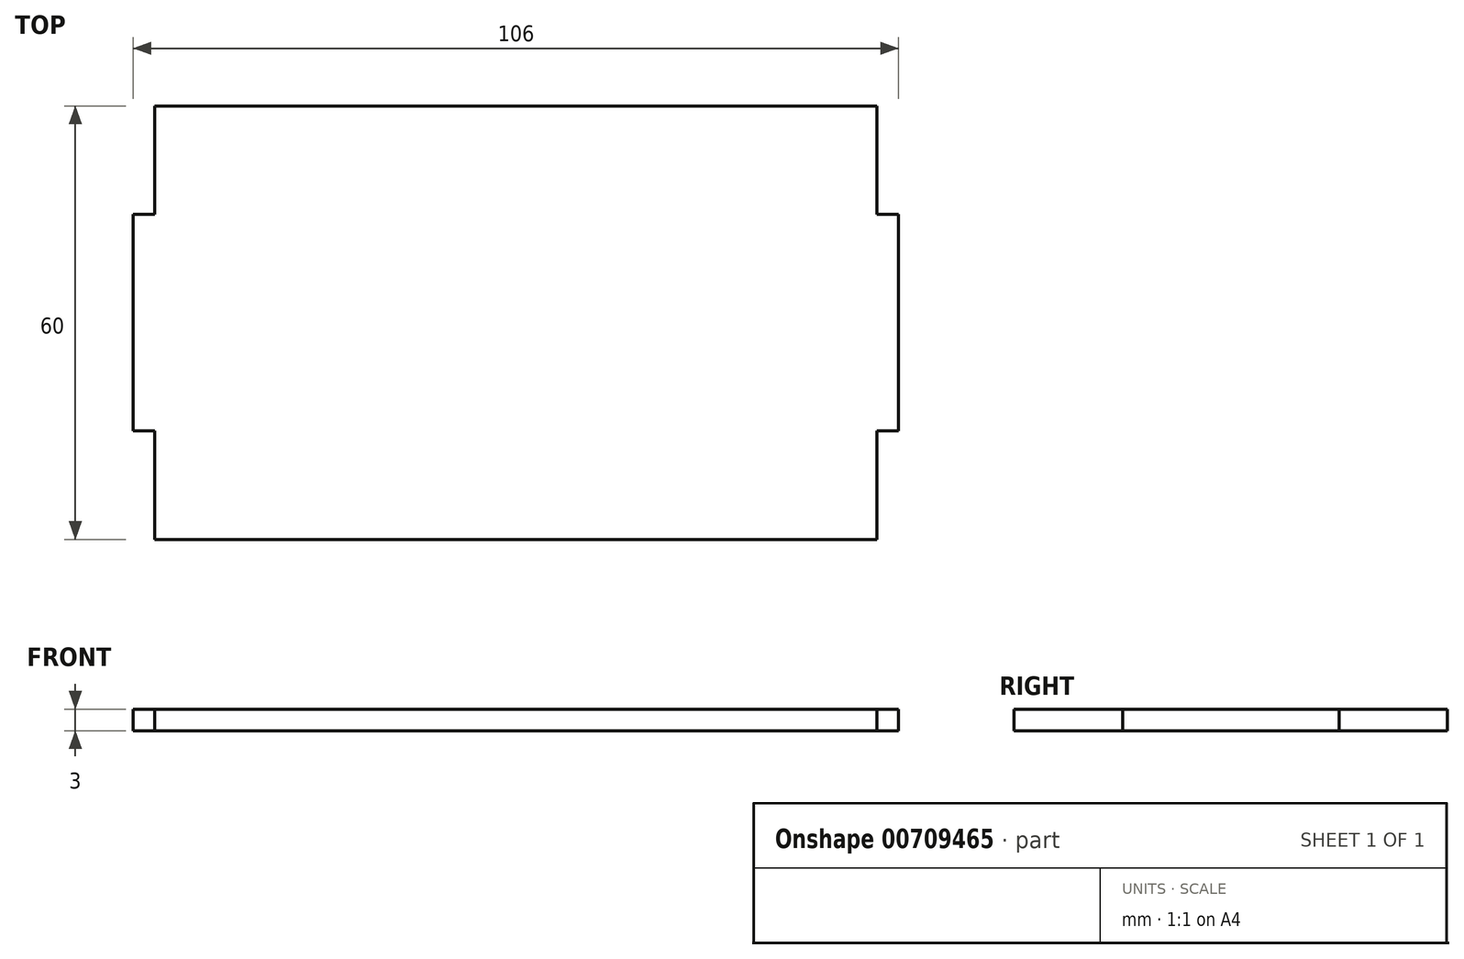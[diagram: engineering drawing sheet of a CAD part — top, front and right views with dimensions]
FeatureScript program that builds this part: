
annotation { "Feature Type Name" : "Feature", "Feature Type Description" : "" }
export const myFeature = defineFeature(function(context is Context, id is Id, definition is map)
    precondition{}
    {
        {
            var Q0;
            Q0=qCreatedBy(makeId("Top.planeOp"),FACE);
            var sketch = newSketch(context, id + "F0", { "sketchPlane" : qUnion([Q0])});
            skLineSegment(sketch, "E0.bottom", {"start": v(-50, 30) * mm, "end": v(50, 30) * mm});
            skLineSegment(sketch, "E0.top", {"start": v(-50, -30) * mm, "end": v(50, -30) * mm});
            skLineSegment(sketch, "E0.left", {"start": v(-50, 30) * mm, "end": v(-50, -30) * mm});
            skLineSegment(sketch, "E0.right", {"start": v(50, 30) * mm, "end": v(50, -30) * mm});
            skPoint(sketch, "E0.middle", {"position": v(0, 0) * mm});
            skLineSegment(sketch, "E1.bottom", {"start": v(-50, 15) * mm, "end": v(-53, 15) * mm});
            skLineSegment(sketch, "E1.top", {"start": v(-50, -15) * mm, "end": v(-53, -15) * mm});
            skLineSegment(sketch, "E1.left", {"start": v(-50, 15) * mm, "end": v(-50, -15) * mm});
            skLineSegment(sketch, "E1.right", {"start": v(-53, 15) * mm, "end": v(-53, -15) * mm});
            skLineSegment(sketch, "E2.MirrorCS", {"start": v(53, 15) * mm, "end": v(53, -15) * mm});
            skLineSegment(sketch, "E3.MirrorCS", {"start": v(50, 15) * mm, "end": v(53, 15) * mm});
            skLineSegment(sketch, "E4.MirrorCS", {"start": v(50, -15) * mm, "end": v(53, -15) * mm});
            skSolve(sketch);
        }
        {
            var Q0;
            Q0 = qSketchRegion(id + "F0", true);
            extrude(context, id + "F1", {"entities" : qUnion([Q0]), "depth" : 3 * mm, "offsetDistance" : 25 * mm});
        }
    });
